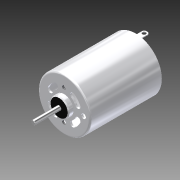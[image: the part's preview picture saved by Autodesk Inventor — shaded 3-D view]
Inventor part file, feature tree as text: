
AUTODESK INVENTOR PART (.ipt)
format: ipt  version: 2011 (Build 150239000, 239)  size: 247,296 bytes
history: native  units: mm
features: extrude x8, sketch x7, fillet x5, chamfer x3, hole x2, shell x1, mirror x1, plane x1, pattern_circular x1
ambient origin geometry x8: Origin, YZ Plane, XZ Plane, XY Plane, X Axis, Y Axis, Z Axis, Center Point
bodies: Solid1 (feature_tree)
feature tree (29):
  extrude  "Extrusion1"  Depth=37.8mm TaperAngle=0.0deg
  fillet  "Fillet1"  Radius=10.0mm
  shell  "Shell1"  Thickness=2.6mm
  extrude  "Extrusion2"  Depth=13.8mm TaperAngle=0.0deg
  extrude  "Extrusion3"  Depth=22.6mm
  sketch  "Sketch4"  dims[d11=0.4mm d12=3.0mm]
  extrude  "Extrusion4"  Depth=3.0mm
  extrude  "Extrusion5"  Depth=1.0mm
  extrude  "Terminal"  Depth=2.0mm
  chamfer  "Chamfer3"  Distance=3.490659mm
  hole  "Hole2"  [1 undecoded]
  extrude  "Extrusion7"  Depth=1.0mm
  mirror  "Mirror1"
  chamfer  "Chamfer1"  Distance=7.0mm
  chamfer  "Chamfer2"  Distance=7.0mm
  plane  "Work Plane1"
  hole  "Hole1"  [1 undecoded]
  pattern_circular  "Circular Pattern1"  [2 undecoded]
  fillet  "Fillet2"  Radius=6.0mm
  fillet  "Fillet3"  Radius=1.0mm
  fillet  "Fillet4"  Radius=4.0mm
  fillet  "Fillet5"  Radius=0.5mm
  extrude  "Extrusion9"  Depth=1.0mm
  sketch  "Sketch1"  dims[d0=27.7mm d1=37.8mm d2=0.0mm d3=10.0mm d4=2.6mm d5=0.0mm]
  sketch  "Sketch2"  dims[d6=2.3mm d7=13.8mm d8=0.0mm]
  sketch  "Sketch3"  dims[d9=10.0mm d10=22.6mm]
  sketch  "Sketch6"  dims[d13=19.0mm d14=1.0mm d15=1.5mm d16=8.37758mm]
  sketch  "Sketch7"  dims[d17=4.363323mm d18=2.0mm]
  sketch  "Sketch8"  dims[d19=15.0mm d20=3.490659mm d21=1.0mm d22=1.0mm d23=7.0mm d24=7.0mm d25=0.5mm d26=0.0mm d27=2.6mm d28=0.0mm d29=6.0mm d30=0.0mm d31=1.0mm d32=4.0mm d33=0.0mm d34=0.5mm d35=2.0mm d36=45.0deg d37=1.0mm d38=32.9mm d44=8.0mm d45=2.113mm d46=6.0mm d47=4.0mm d48=2.0mm d49=90.0deg d50=8.0mm d51=20.594885mm d52=20.0mm d53=360.0deg d55=0.2mm d56=2.0mm d57=45.0deg d58=0.75mm d59=2.0mm d60=45.0deg d61=4.5mm d62=2.0mm d63=6.0mm d64=4.0mm d65=2.0mm d66=90.0deg d67=8.0mm d68=20.594885mm d146=10.0mm d147=0.0mm]
note: 4 required parameter values undecoded (feature->parameter linkage not recoverable at this tier; creation-order binding heuristic only, values carry confidence <= 0.55)
